# Revit family: PIF_AS Eckdoppelabzweig_Wavin
name_source: partatom
category: Rohrformteile
units: mm (PartAtom-declared; Revit-internal decimal feet)

## family parameters
Arbeitsebenenbasiert = Nein
Beim Laden mit Abzugskörper schneiden = Nein
Bemaßung runder Anschluss = Durchmesser verwenden
Gemeinsam genutzt = Ja
Immer vertikal = Ja
OmniClass-Nummer = 23.60.30.11.14
OmniClass-Titel = Pipework Fittings
Teiletyp = Kreuzstück

## types (2) — shared parameters
Beschreibung = AS Corner branch
Hersteller = Wavin
IfcDescription = AS Corner branch
IfcExportAs = IfcPipeFitting
IfcExportType = JUNCTION
LOD = LOD400
URL = http://de.wavin.com
Verlustberechnungsmethode = Nicht definiert
localisation = GE
material = Polypropylene - Astolan, White, RAL9010
product_serie = Wavin AS
region_index = 4

## per-type parameters (varying)
| type | coupler |
| mit_Muffe | Nein |
| ohne_Muffe | Ja |

## geometry (parser evidence)
native form markers: Sweep x8
no freeform markers — native parametric forms only
